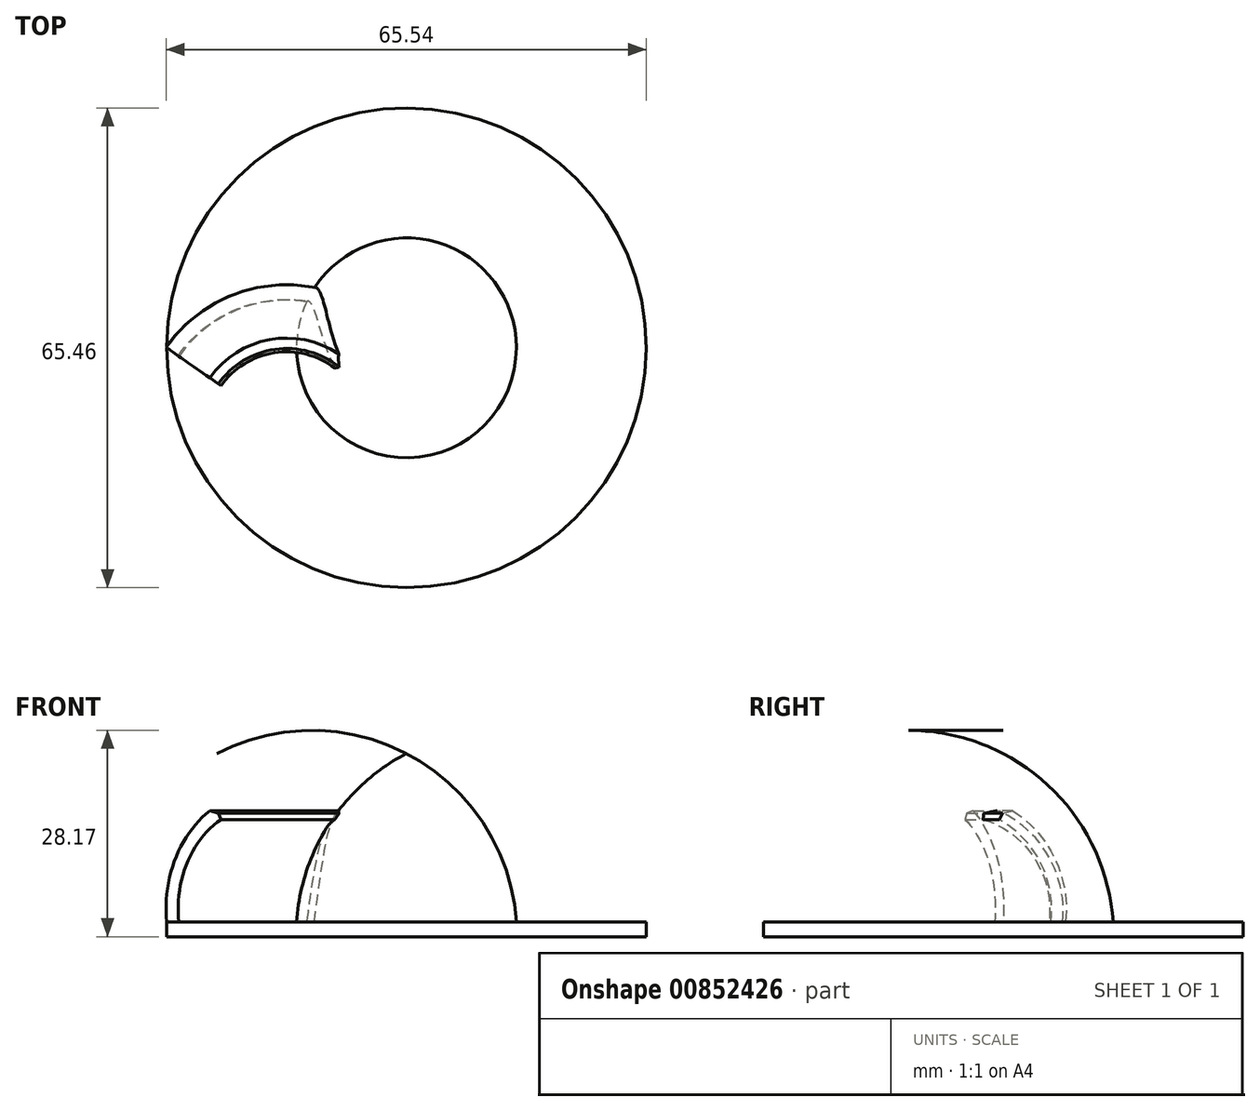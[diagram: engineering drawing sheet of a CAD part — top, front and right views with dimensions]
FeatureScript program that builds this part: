
annotation { "Feature Type Name" : "Feature", "Feature Type Description" : "" }
export const myFeature = defineFeature(function(context is Context, id is Id, definition is map)
    precondition{}
    {
        {
            var Q0;
            Q0=qCreatedBy(makeId("Top.planeOp"),FACE);
            var sketch = newSketch(context, id + "F0", { "sketchPlane" : qUnion([Q0])});
            skCircle(sketch, "E0", {"center": v(0, 0) * mm, "radius": 32.73 * mm});
            skSolve(sketch);
        }
        {
            var Q0;
            Q0=makeQuery(id+"F0.imprint","IMPRINT",FACE,{"disambiguationData":[TD([[makeQuery(id+"F0.imprint","IMPRINT",EDGE,{"derivedFrom":sQuery(id+"F0.wireOp",EDGE,"E0")}),1.0]])]});
            extrude(context, id + "F1", {"entities" : qUnion([Q0]), "depth" : 2 * mm, "offsetDistance" : 25 * mm});
        }
        {
            var Q0;
            Q0=qCreatedBy(makeId("Front.planeOp"),FACE);
            var sketch = newSketch(context, id + "F2", { "sketchPlane" : qUnion([Q0])});
            skLineSegment(sketch, "E1", {"start": v(0, 0) * mm, "end": v(0, 25) * mm});
            skArc(sketch, "E2", {"start": v(0, 25) * mm, "mid": v(-10.51, 15.46) * mm, "end": v(-15, 2) * mm});
            skLineSegment(sketch, "E3", {"start": v(-15, 2) * mm, "end": v(-15, 0) * mm});
            skLineSegment(sketch, "E4", {"start": v(-15, 0) * mm, "end": v(0, 0) * mm});
            skSolve(sketch);
        }
        {
            var Q0;
            Q0=makeQuery(id+"F2.imprint","IMPRINT",FACE,{"disambiguationData":[TD([[makeQuery(id+"F2.imprint","IMPRINT",EDGE,{"derivedFrom":sQuery(id+"F2.wireOp",EDGE,"E1")}),1.0]])]});
            var Q1;
            Q1=sQuery(id+"F2.wireOp",EDGE,"E1");
            revolve(context, id + "F3", {"operationType" : NewBodyOperationType.ADD, "surfaceOperationType" : NewSurfaceOperationType.NEW, "entities" : qUnion([Q0]), "axis" : qUnion([Q1]), "revolveType" : RevolveType.FULL});
        }
        {
            var Q0;
            Q0=makeQuery(id+"F1.opExtrude","CAP_FACE",FACE,{"disambiguationData":[OSD([sQuery(id+"F0.wireOp",EDGE,"E0")])],"isStart":false});
            var sketch = newSketch(context, id + "F4", { "sketchPlane" : qUnion([Q0])});
            skArc(sketch, "E5", {"start": v(0, 0) * mm, "mid": v(-16.36, 8.5) * mm, "end": v(-32.73, 0) * mm});
            skSolve(sketch);
        }
        {
            var Q0;
            Q0=sQuery(id+"F4.wireOp",EDGE,"E5");
            var Q1;
            Q1=sQuery(id+"F4.wireOp",VERTEX,"E5.end");
            cPlane(context, id + "F5", {"entities" : qUnion([Q0, Q1]), "cplaneType" : CPlaneType.CURVE_POINT, "offset" : 25 * mm, "width" : 150 * mm, "height" : 150 * mm});
        }
        {
            var Q0;
            Q0=qCreatedBy(id+"F5.planeOp",FACE);
            var sketch = newSketch(context, id + "F6", { "sketchPlane" : qUnion([Q0])});
            skLineSegment(sketch, "E6", {"start": v(-26.78, 2) * mm, "end": v(-24.76, 2) * mm});
            skArc(sketch, "E7", {"start": v(-17.72, 16) * mm, "mid": v(-23.39, 10.08) * mm, "end": v(-24.76, 2) * mm});
            skArc(sketch, "E8.0", {"start": v(-18.67, 17.76) * mm, "mid": v(-25.1, 11.1) * mm, "end": v(-26.78, 2) * mm});
            skLineSegment(sketch, "E9", {"start": v(-18.67, 17.76) * mm, "end": v(-17.72, 16) * mm});
            skSolve(sketch);
        }
        {
            var Q0;
            Q0 = qSketchRegion(id + "F6", true);
            var Q1;
            Q1 = qConstructionFilter(qBodyType(qCreatedBy(id + "F4" ,EDGE), BodyType.WIRE), ConstructionObject.NO);
            sweep(context, id + "F7", {"operationType" : NewBodyOperationType.ADD, "profiles" : qUnion([Q0]), "path" : qUnion([Q1])});
        }
        {
            var Q0;
            Q0=makeQuery(id+"F7.opSweep","SWEPT_EDGE",EDGE,{"disambiguationData":[OSD([sQuery(id+"F4.wireOp",EDGE,"E5"),sQuery(id+"F6.wireOp",EDGE,"E8.0"),sQuery(id+"F6.wireOp",EDGE,"E9")])]});
            chamfer(context, id + "F8", {"entities" : qUnion([Q0]), "width" : 1 * mm, "tangentPropagation" : true});
        }
    });
